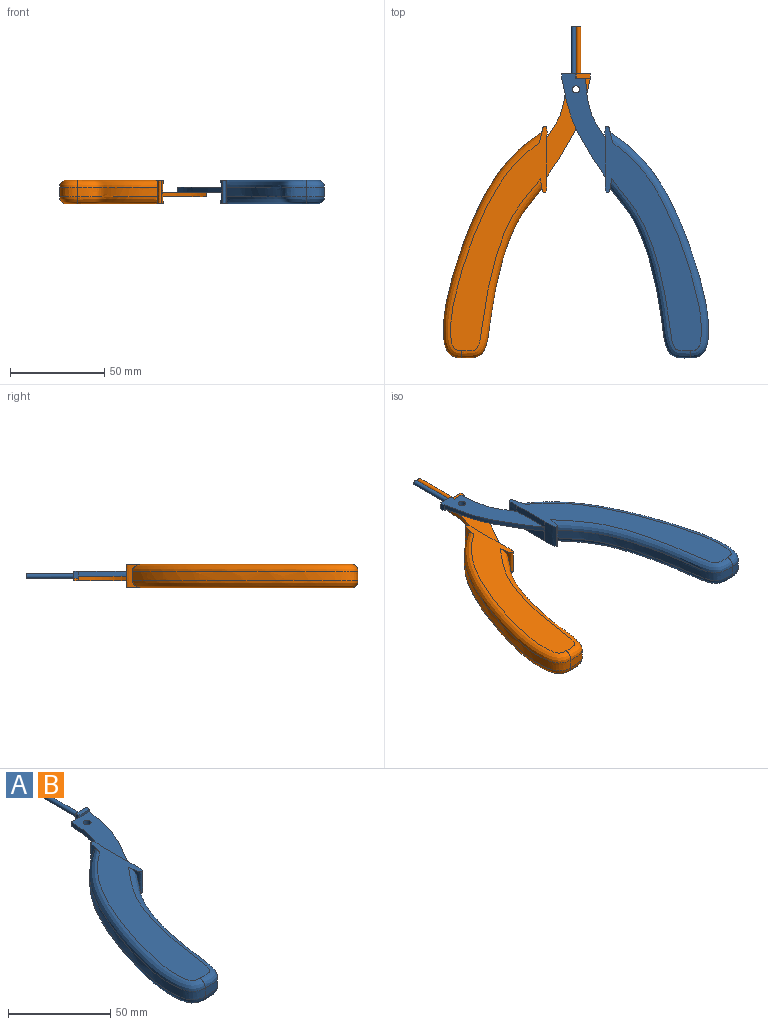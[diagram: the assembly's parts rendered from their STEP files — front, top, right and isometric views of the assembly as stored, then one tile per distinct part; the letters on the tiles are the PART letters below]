
ASSEMBLY  parts=2 mates=1
PART A: 28 faces, bbox 78.1x176.5x12.7 mm
  f0: plane 7.62x3.81mm, normal (0,1,0), area 23.6mm2, adj f1,f22,f23,f24,f26
  f1: plane 54.96x23.17mm, normal (0,0,-1), area 523.2mm2, adj f0,f2,f3,f4,f6,f15,f22,f23
  f2: plane 5.08x2.54mm, normal (0,1,0), area 12.9mm2, adj f1,f3,f5,f23
  f3: extruded ~31.5x10.47mm, area 85.9mm2, adj f1,f2,f5,f8
  f4: extruded ~52.42x23.17mm, area 147.1mm2, adj f1,f5,f13,f22
  f5: plane 52.42x23.17mm, normal (0,0,1), area 503.8mm2, adj f2,f3,f4,f6,f7,f21
  f6: cylinder r=1.91mm len=3.81mm, axis (0,0,1), area 30.4mm2, adj f1,f5
  f7: plane 20.92x6.35mm, normal (1,0,0), area 132.9mm2, adj f5,f8,f13,f14
  f8: extruded ~12.7x6.08mm, area 83.1mm2, adj f3,f7,f9,f14,f15,f16
  f9: extruded ~12.7x8.72mm, area 73.8mm2, adj f8,f10,f14,f16,f17,f19
  f10: extruded ~119.93x52.28mm, area 719mm2, adj f9,f11,f17,f19
  f11: extruded ~90.15x42.73mm, area 540.9mm2, adj f10,f12,f18,f20
  f12: extruded ~12.7x7.11mm, area 62.6mm2, adj f11,f13,f14,f16,f18,f20
  f13: extruded ~12.7x7.94mm, area 102.2mm2, adj f4,f7,f12,f14,f15,f16
  f14: plane 119.46x51.4mm, normal (0,0,1), area 1834.7mm2, adj f7,f8,f9,f12,f13,f17,f18
  f15: plane 20.92x3.81mm, normal (1,0,0), area 79.7mm2, adj f1,f8,f13,f16
  f16: plane 119.46x51.4mm, normal (0,0,-1), area 1834.7mm2, adj f8,f9,f12,f13,f15,f19,f20
  f17: bspline ~120.54x55.29mm, area 813.6mm2, adj f9,f10,f14,f18
  f18: bspline ~98.32x47.9mm, area 642.3mm2, adj f11,f12,f14,f17
  f19: bspline ~120.54x55.29mm, area 813.5mm2, adj f9,f10,f16,f20
  f20: bspline ~98.32x47.9mm, area 641.9mm2, adj f11,f12,f16,f19
  f21: plane 7.62x1.27mm, normal (0,-1,0), area 9.7mm2, adj f5,f22,f23,f24
  f22: plane 3.81x2.54mm, normal (1,0,0), area 9.7mm2, adj f0,f1,f4,f21,f24
  f23: plane 3.81x2.54mm, normal (-1,0,0), area 9.7mm2, adj f0,f1,f2,f21,f24,f25
  f24: plane 7.62x2.54mm, normal (0,0,1), area 19.4mm2, adj f0,f21,f22,f23,f25
  f25: plane 1.27x1.27mm, normal (0,1,0), area 0.3mm2, adj f23,f24,f26
  f26: cylinder r=1.27mm len=25.4mm, axis (0,-1,0), area 202.7mm2, adj f0,f25,f27
  f27: plane 2.54x2.54mm, normal (0,1,0), area 5.1mm2, adj f26
PART B: same geometry as A
PLACE A rot(axis=(0,1,0),180deg) t=(13.31,-1.28,7.77)mm
PLACE B t=(3.18,-1.28,2.69)mm
MATE revolute A.f6 <-> B.f6  axis (0,0,-1) through (8.24,-7.06,5.23)mm
